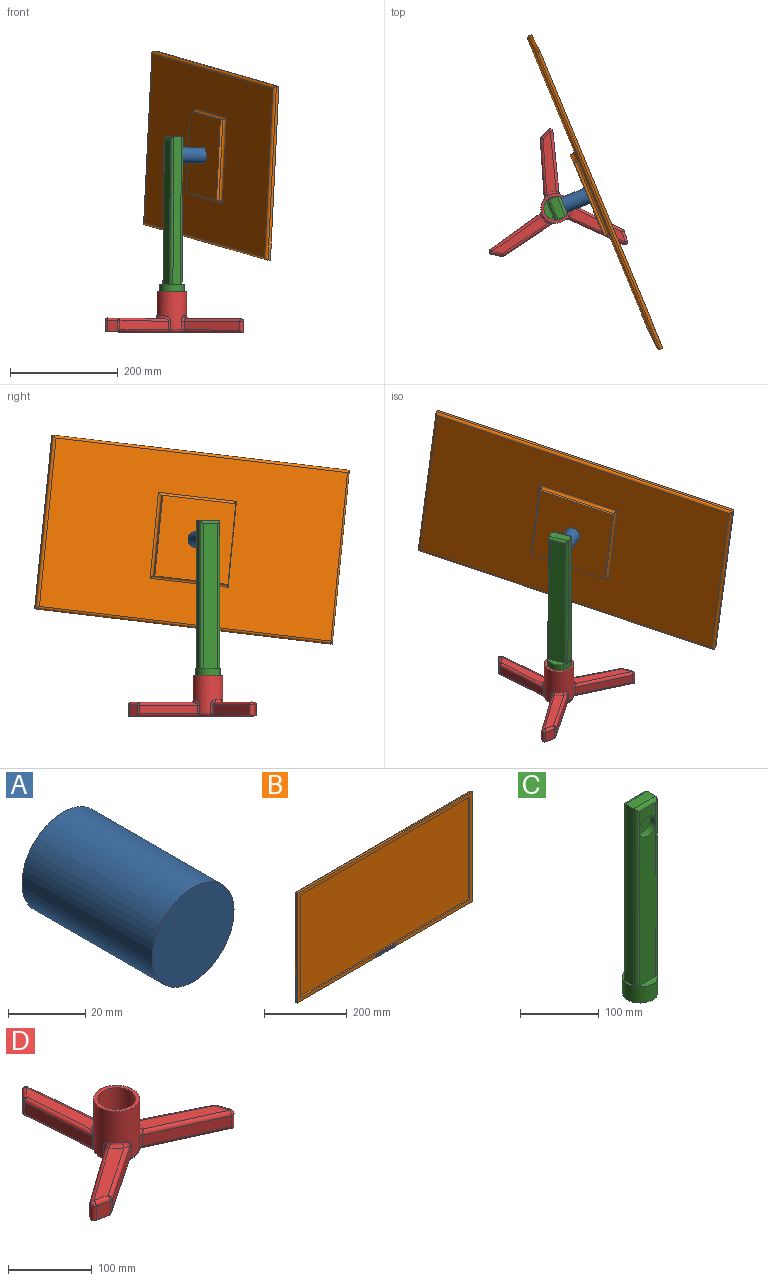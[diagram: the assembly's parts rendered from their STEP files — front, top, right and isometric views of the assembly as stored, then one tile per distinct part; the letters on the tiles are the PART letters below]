
ASSEMBLY  parts=4 mates=3
PART A: 3 faces, bbox 30x47.7x30 mm
  f0: cylinder r=15mm len=47.7mm, axis (0,1,0), area 4495.6mm2, adj f1,f2
  f1: plane 30x30mm, normal (0,-1,0), area 706.9mm2, adj f0
  f2: plane 30x30mm, normal (0,1,0), area 706.9mm2, adj f0
PART B: 199 faces, bbox 600.6x21x326.2 mm
  f0: plane 590.61x316.14mm, normal (0,1,0), area 160454.4mm2, adj f191,f192,f193,f194,f195,f196,f197,f198
  f1: plane 580x5mm, normal (0,0,-1), area 2900mm2, adj f2,f8,f9,f10
  f2: plane 305x5mm, normal (-1,0,0), area 1525mm2, adj f1,f3,f9,f10
  f3: plane 580x5mm, normal (0,0,1), area 2900mm2, adj f2,f8,f9,f10
  f4: plane 325x5mm, normal (1,0,0), area 1625mm2, adj f5,f7,f9,f196
  f5: plane 600x5mm, normal (0,0,1), area 3000mm2, adj f4,f6,f9,f195
  f6: plane 325x5mm, normal (-1,0,0), area 1625mm2, adj f5,f7,f9,f197
  f7: plane 600x5mm, normal (0,0,-1), area 3000mm2, adj f4,f6,f9,f198
  f8: plane 305x5mm, normal (1,0,0), area 1525mm2, adj f1,f3,f9,f10
  f9: plane 600.63x326.16mm, normal (0,-1,0), area 17876.4mm2, adj f1,f2,f3,f4,f5,f6,f7,f8
  f10: plane 580.59x306.12mm, normal (0,-1,0), area 176900mm2, adj f1,f2,f3,f8
  f11: plane 4.15x3.06mm, normal (0.8,0,0.59), area 5.2mm2, adj f9,f12,f22,f23
  f12: plane 3.18x2.95mm, normal (0.73,0,-0.68), area 4.3mm2, adj f9,f11,f13,f23
  f13: plane 1.01x1mm, normal (0,0,1), area 1mm2, adj f9,f12,f14,f23
  f14: plane 3.63x3.32mm, normal (-0.74,0,0.67), area 4.9mm2, adj f9,f13,f15,f23
  f15: plane 3.63x1mm, normal (1,0,0), area 3.6mm2, adj f9,f14,f16,f23
  f16: plane 1x0.85mm, normal (0,0,1), area 0.9mm2, adj f9,f15,f17,f23
  f17: plane 7.33x1mm, normal (-1,0,0), area 7.3mm2, adj f9,f16,f18,f23
  f18: plane 1x0.85mm, normal (0,0,-1), area 0.9mm2, adj f9,f17,f19,f23
  f19: plane 2.87x1mm, normal (1,0,0), area 2.9mm2, adj f9,f18,f20,f23
  f20: plane 1x0.77mm, normal (0.66,0,-0.75), area 1mm2, adj f9,f19,f21,f23
  f21: plane 3.55x2.67mm, normal (-0.8,0,-0.6), area 4.4mm2, adj f9,f20,f22,f23
  f22: plane 1x1mm, normal (0,0,-1), area 1mm2, adj f9,f11,f21,f23
  f23: plane 7.33x5.29mm, normal (0,-1,0), area 14.2mm2, adj f11,f12,f13,f14,f15,f16,f17,f18
  f24: plane 1x0.76mm, normal (-1,0,0), area 0.8mm2, adj f9,f25,f43,f44
  f25: plane 1.64x1mm, normal (0,0,-1), area 1.6mm2, adj f9,f24,f26,f44
  f26: plane 2.26x1mm, normal (-1,0,0), area 2.3mm2, adj f9,f25,f27,f44
  f27: extruded ~1.49x1mm, area 1.5mm2, adj f9,f26,f28,f44
  f28: extruded ~2.13x1mm, area 2.3mm2, adj f9,f27,f29,f44
  f29: extruded ~2.25x1mm, area 2.4mm2, adj f9,f28,f30,f44
  f30: extruded ~2.21x1mm, area 2.4mm2, adj f9,f29,f31,f44
  f31: extruded ~2.09x1mm, area 2.3mm2, adj f9,f30,f32,f44
  f32: extruded ~1.91x1mm, area 2mm2, adj f9,f31,f33,f44
  f33: plane 1x0.75mm, normal (0.92,0,-0.4), area 0.8mm2, adj f9,f32,f34,f44
  f34: extruded ~2.19x1mm, area 2.2mm2, adj f9,f33,f35,f44
  f35: extruded ~2.02x1mm, area 2.1mm2, adj f9,f34,f36,f44
  f36: extruded ~1.32x1.31mm, area 1.9mm2, adj f9,f35,f37,f44
  f37: extruded ~2x1mm, area 2.1mm2, adj f9,f36,f38,f44
  f38: extruded ~2.77x1mm, area 3mm2, adj f9,f37,f39,f44
  f39: extruded ~2.59x1mm, area 2.9mm2, adj f9,f38,f40,f44
  f40: extruded ~1.39x1mm, area 1.4mm2, adj f9,f39,f41,f44
  f41: extruded ~1.18x1mm, area 1.2mm2, adj f9,f40,f42,f44
  f42: plane 3.56x1mm, normal (1,0,0), area 3.6mm2, adj f9,f41,f43,f44
  f43: plane 2.49x1mm, normal (0,0,1), area 2.5mm2, adj f9,f24,f42,f44
  f44: plane 7.53x6.1mm, normal (0,-1,0), area 16.3mm2, adj f24,f25,f26,f27,f28,f29,f30,f31
  f45: plane 7.33x1mm, normal (-1,0,0), area 7.3mm2, adj f9,f46,f69,f70
  f46: plane 2.56x1mm, normal (0,0,-1), area 2.6mm2, adj f9,f45,f47,f70
  f47: extruded ~1.86x1mm, area 2mm2, adj f9,f46,f48,f70
  f48: extruded ~1.53x1mm, area 1.7mm2, adj f9,f47,f49,f70
  f49: extruded ~1.76x1.67mm, area 2.7mm2, adj f9,f48,f50,f70
  f50: plane 1x0.05mm, normal (1,0,0), area 0mm2, adj f9,f49,f51,f70
  f51: extruded ~1.06x1mm, area 1.2mm2, adj f9,f50,f52,f70
  f52: extruded ~1.08x1mm, area 1.2mm2, adj f9,f51,f53,f70
  f53: extruded ~1.38x1mm, area 1.6mm2, adj f9,f52,f54,f70
  f54: extruded ~2.11x1mm, area 2.2mm2, adj f9,f53,f69,f70
  f55: plane 2.4x1mm, normal (1,0,0), area 2.4mm2, adj f56,f67,f70,f72
  f56: plane 1.25x1mm, normal (0,0,-1), area 1.3mm2, adj f55,f57,f70,f72
  f57: extruded ~1.4x1mm, area 1.4mm2, adj f56,f58,f70,f72
  f58: extruded ~1x0.89mm, area 1mm2, adj f57,f59,f70,f72
  f59: extruded ~1x0.95mm, area 1.1mm2, adj f58,f60,f70,f72
  f60: extruded ~1.3x1mm, area 1.3mm2, adj f59,f67,f70,f72
  f61: plane 1.46x1mm, normal (0,0,-1), area 1.5mm2, adj f62,f68,f70,f71
  f62: extruded ~1.4x1mm, area 1.5mm2, adj f61,f63,f70,f71
  f63: extruded ~1x1mm, area 1.1mm2, adj f62,f64,f70,f71
  f64: extruded ~1.08x1mm, area 1.2mm2, adj f63,f65,f70,f71
  f65: extruded ~1.34x1mm, area 1.4mm2, adj f64,f66,f70,f71
  f66: plane 1.53x1mm, normal (0,0,1), area 1.5mm2, adj f65,f68,f70,f71
  f67: plane 1.4x1mm, normal (0,0,1), area 1.4mm2, adj f55,f60,f70,f72
  f68: plane 2.74x1mm, normal (1,0,0), area 2.7mm2, adj f61,f66,f70,f71
  f69: plane 2.07x1mm, normal (0,0,1), area 2.1mm2, adj f9,f45,f54,f70
  f70: plane 7.33x5.08mm, normal (0,-1,0), area 18.3mm2, adj f45,f46,f47,f48,f49,f50,f51,f52
  f71: plane 3.31x2.74mm, normal (0,-1,0), area 8.3mm2, adj f61,f62,f63,f64,f65,f66,f68
  f72: plane 3.1x2.4mm, normal (0,-1,0), area 6.8mm2, adj f55,f56,f57,f58,f59,f60,f67
  f73: extruded ~2.75x2.14mm, area 4mm2, adj f9,f74,f87,f88
  f74: plane 1.9x1mm, normal (0,0,1), area 1.9mm2, adj f9,f73,f75,f88
  f75: plane 7.33x1mm, normal (-1,0,0), area 7.3mm2, adj f9,f74,f76,f88
  f76: plane 1x0.85mm, normal (0,0,-1), area 0.9mm2, adj f9,f75,f77,f88
  f77: plane 2.88x1mm, normal (1,0,0), area 2.9mm2, adj f9,f76,f78,f88
  f78: plane 1x0.86mm, normal (0,0,-1), area 0.9mm2, adj f9,f77,f79,f88
  f79: extruded ~2.17x1mm, area 2.3mm2, adj f9,f78,f87,f88
  f80: plane 2.98x1mm, normal (1,0,0), area 3mm2, adj f81,f86,f88,f89
  f81: plane 1x0.95mm, normal (0,0,-1), area 1mm2, adj f80,f82,f88,f89
  f82: extruded ~1.48x1mm, area 1.6mm2, adj f81,f83,f88,f89
  f83: extruded ~1.08x1mm, area 1.2mm2, adj f82,f84,f88,f89
  f84: extruded ~1.17x1mm, area 1.3mm2, adj f83,f85,f88,f89
  f85: extruded ~1.64x1mm, area 1.7mm2, adj f84,f86,f88,f89
  f86: plane 1x0.77mm, normal (0,0,1), area 0.8mm2, adj f80,f85,f88,f89
  f87: extruded ~1.71x1mm, area 1.9mm2, adj f9,f73,f79,f88
  f88: plane 7.33x4.65mm, normal (0,-1,0), area 13.2mm2, adj f73,f74,f75,f76,f77,f78,f79,f80
  f89: plane 2.98x2.91mm, normal (0,-1,0), area 7.7mm2, adj f80,f81,f82,f83,f84,f85,f86
  f90: plane 1.53x1mm, normal (0,0,-1), area 1.5mm2, adj f9,f91,f107,f108
  f91: plane 3.05x1.77mm, normal (-0.86,0,-0.5), area 3.5mm2, adj f9,f90,f92,f108
  f92: plane 1.01x1mm, normal (0,0,-1), area 1mm2, adj f9,f91,f93,f108
  f93: plane 3.29x1.99mm, normal (0.86,0,0.52), area 3.8mm2, adj f9,f92,f94,f108
  f94: extruded ~1.97x1.47mm, area 2.6mm2, adj f9,f93,f95,f108
  f95: extruded ~1.55x1mm, area 1.7mm2, adj f9,f94,f96,f108
  f96: extruded ~1.99x1mm, area 2.1mm2, adj f9,f95,f97,f108
  f97: plane 2.01x1mm, normal (0,0,1), area 2mm2, adj f9,f96,f98,f108
  f98: plane 7.33x1mm, normal (-1,0,0), area 7.3mm2, adj f9,f97,f99,f108
  f99: plane 1x0.85mm, normal (0,0,-1), area 0.9mm2, adj f9,f98,f107,f108
  f100: plane 2.8x1mm, normal (1,0,0), area 2.8mm2, adj f101,f106,f108,f109
  f101: plane 1.11x1mm, normal (0,0,-1), area 1.1mm2, adj f100,f102,f108,f109
  f102: extruded ~1.38x1mm, area 1.4mm2, adj f101,f103,f108,f109
  f103: extruded ~1.05x1mm, area 1.2mm2, adj f102,f104,f108,f109
  f104: extruded ~1.08x1mm, area 1.2mm2, adj f103,f105,f108,f109
  f105: extruded ~1.32x1mm, area 1.4mm2, adj f104,f106,f108,f109
  f106: plane 1.17x1mm, normal (0,0,1), area 1.2mm2, adj f100,f105,f108,f109
  f107: plane 3.05x1mm, normal (1,0,0), area 3mm2, adj f9,f90,f99,f108
  f108: plane 7.33x5.16mm, normal (0,-1,0), area 16.1mm2, adj f90,f91,f92,f93,f94,f95,f96,f97
  f109: plane 2.91x2.8mm, normal (0,-1,0), area 7.4mm2, adj f100,f101,f102,f103,f104,f105,f106
  f110: extruded ~2.77x1mm, area 3mm2, adj f9,f111,f125,f126
  f111: extruded ~2.47x1mm, area 2.7mm2, adj f9,f110,f112,f126
  f112: extruded ~2.51x1mm, area 2.8mm2, adj f9,f111,f113,f126
  f113: extruded ~2.78x1mm, area 3mm2, adj f9,f112,f114,f126
  f114: extruded ~2.8x1mm, area 3mm2, adj f9,f113,f115,f126
  f115: extruded ~2.5x1mm, area 2.8mm2, adj f9,f114,f116,f126
  f116: extruded ~2.47x1.01mm, area 2.8mm2, adj f9,f115,f125,f126
  f117: extruded ~2.24x1mm, area 2.4mm2, adj f118,f124,f126,f127
  f118: extruded ~1.85x1mm, area 2.1mm2, adj f117,f119,f126,f127
  f119: extruded ~1.83x1mm, area 2.1mm2, adj f118,f120,f126,f127
  f120: extruded ~2.24x1mm, area 2.4mm2, adj f119,f121,f126,f127
  f121: extruded ~2.26x1mm, area 2.4mm2, adj f120,f122,f126,f127
  f122: extruded ~1.84x1mm, area 2.1mm2, adj f121,f123,f126,f127
  f123: extruded ~1.84x1mm, area 2.1mm2, adj f122,f124,f126,f127
  f124: extruded ~2.26x1mm, area 2.4mm2, adj f117,f123,f126,f127
  f125: extruded ~2.77x1mm, area 3mm2, adj f9,f110,f116,f126
  f126: plane 7.55x6.74mm, normal (0,-1,0), area 17mm2, adj f110,f111,f112,f113,f114,f115,f116,f117
  f127: plane 6.04x4.94mm, normal (0,-1,0), area 24.7mm2, adj f117,f118,f119,f120,f121,f122,f123,f124
  f128: extruded ~2.65x1mm, area 2.9mm2, adj f9,f129,f141,f142
  f129: extruded ~2.66x1mm, area 2.9mm2, adj f9,f128,f130,f142
  f130: plane 2.25x1mm, normal (0,0,1), area 2.2mm2, adj f9,f129,f131,f142
  f131: plane 7.33x1mm, normal (-1,0,0), area 7.3mm2, adj f9,f130,f132,f142
  f132: plane 2.03x1mm, normal (0,0,-1), area 2mm2, adj f9,f131,f133,f142
  f133: extruded ~2.83x1mm, area 3.1mm2, adj f9,f132,f141,f142
  f134: extruded ~2.22x1mm, area 2.4mm2, adj f135,f140,f142,f143
  f135: extruded ~2.29x1mm, area 2.5mm2, adj f134,f136,f142,f143
  f136: plane 1.04x1mm, normal (0,0,1), area 1mm2, adj f135,f137,f142,f143
  f137: plane 5.85x1mm, normal (1,0,0), area 5.9mm2, adj f136,f138,f142,f143
  f138: plane 1.24x1mm, normal (0,0,-1), area 1.2mm2, adj f137,f139,f142,f143
  f139: extruded ~2.14x1mm, area 2.3mm2, adj f138,f140,f142,f143
  f140: extruded ~2.16x1mm, area 2.3mm2, adj f134,f139,f142,f143
  f141: extruded ~2.77x1mm, area 3mm2, adj f9,f128,f133,f142
  f142: plane 7.33x5.85mm, normal (0,-1,0), area 17mm2, adj f128,f129,f130,f131,f132,f133,f134,f135
  f143: plane 5.85x4.1mm, normal (0,-1,0), area 21.1mm2, adj f134,f135,f136,f137,f138,f139,f140
  f144: plane 1x0.85mm, normal (0,0,1), area 0.9mm2, adj f9,f145,f157,f158
  f145: plane 4.77x1mm, normal (-1,0,0), area 4.8mm2, adj f9,f144,f146,f158
  f146: extruded ~1.42x1mm, area 1.5mm2, adj f9,f145,f147,f158
  f147: extruded ~1.43x1mm, area 1.6mm2, adj f9,f146,f148,f158
  f148: extruded ~1.47x1mm, area 1.6mm2, adj f9,f147,f149,f158
  f149: extruded ~1.41x1mm, area 1.5mm2, adj f9,f148,f150,f158
  f150: plane 4.78x1mm, normal (1,0,0), area 4.8mm2, adj f9,f149,f151,f158
  f151: plane 1x0.85mm, normal (0,0,1), area 0.9mm2, adj f9,f150,f152,f158
  f152: plane 4.72x1mm, normal (-1,0,0), area 4.7mm2, adj f9,f151,f153,f158
  f153: extruded ~1.99x1mm, area 2.2mm2, adj f9,f152,f154,f158
  f154: extruded ~2.05x1mm, area 2.2mm2, adj f9,f153,f155,f158
  f155: extruded ~2.08x1mm, area 2.3mm2, adj f9,f154,f156,f158
  f156: extruded ~1.97x1mm, area 2.2mm2, adj f9,f155,f157,f158
  f157: plane 4.74x1mm, normal (1,0,0), area 4.7mm2, adj f9,f144,f156,f158
  f158: plane 7.43x5.61mm, normal (0,-1,0), area 14.1mm2, adj f144,f145,f146,f147,f148,f149,f150,f151
  f159: extruded ~1.67x1mm, area 1.7mm2, adj f9,f160,f173,f174
  f160: plane 1x0.73mm, normal (0.9,0,-0.44), area 0.8mm2, adj f9,f159,f161,f174
  f161: extruded ~2.01x1mm, area 2.1mm2, adj f9,f160,f162,f174
  f162: extruded ~1.88x1mm, area 2mm2, adj f9,f161,f163,f174
  f163: extruded ~1.31x1.22mm, area 1.8mm2, adj f9,f162,f164,f174
  f164: extruded ~1.98x1mm, area 2mm2, adj f9,f163,f165,f174
  f165: extruded ~2.79x1mm, area 3mm2, adj f9,f164,f166,f174
  f166: extruded ~2.5x1mm, area 2.8mm2, adj f9,f165,f167,f174
  f167: extruded ~1.88x1mm, area 1.9mm2, adj f9,f166,f168,f174
  f168: plane 1x0.75mm, normal (1,0,0), area 0.7mm2, adj f9,f167,f169,f174
  f169: extruded ~1.75x1mm, area 1.8mm2, adj f9,f168,f170,f174
  f170: extruded ~1.92x1mm, area 2.1mm2, adj f9,f169,f171,f174
  f171: extruded ~2.22x1mm, area 2.4mm2, adj f9,f170,f172,f174
  f172: extruded ~2.2x1mm, area 2.4mm2, adj f9,f171,f173,f174
  f173: extruded ~1.91x1mm, area 2.1mm2, adj f9,f159,f172,f174
  f174: plane 7.53x5.54mm, normal (0,-1,0), area 11.7mm2, adj f159,f160,f161,f162,f163,f164,f165,f166
  f175: plane 6.57x1mm, normal (1,0,0), area 6.6mm2, adj f9,f176,f182,f183
  f176: plane 2.32x1mm, normal (0,0,-1), area 2.3mm2, adj f9,f175,f177,f183
  f177: plane 1x0.76mm, normal (1,0,0), area 0.8mm2, adj f9,f176,f178,f183
  f178: plane 5.49x1mm, normal (0,0,1), area 5.5mm2, adj f9,f177,f179,f183
  f179: plane 1x0.76mm, normal (-1,0,0), area 0.8mm2, adj f9,f178,f180,f183
  f180: plane 2.32x1mm, normal (0,0,-1), area 2.3mm2, adj f9,f179,f181,f183
  f181: plane 6.57x1mm, normal (-1,0,0), area 6.6mm2, adj f9,f180,f182,f183
  f182: plane 1x0.85mm, normal (0,0,-1), area 0.9mm2, adj f9,f175,f181,f183
  f183: plane 7.33x5.49mm, normal (0,-1,0), area 9.8mm2, adj f175,f176,f177,f178,f179,f180,f181,f182
  f184: plane 147.83x5mm, normal (0,0,-1), area 739.1mm2, adj f185,f187,f188,f191
  f185: plane 150.91x5mm, normal (1,0,0), area 754.5mm2, adj f184,f186,f188,f192
  f186: plane 147.83x5mm, normal (0,0,1), area 739.1mm2, adj f185,f187,f188,f194
  f187: plane 150.91x5mm, normal (-1,0,0), area 754.5mm2, adj f184,f186,f188,f193
  f188: plane 150.91x147.83mm, normal (0,1,0), area 21601.4mm2, adj f184,f185,f186,f187,f189
  f189: cylinder r=15mm len=30mm, axis (0,1,0), area 942.5mm2, adj f188,f190
  f190: plane 30x30mm, normal (0,1,0), area 706.9mm2, adj f189
  f191: cylinder r=5mm len=157.83mm, axis (1,0,0), area 1189.6mm2, adj f0,f184,f192,f193
  f192: cylinder r=5mm len=160.91mm, axis (0,0,1), area 1213.8mm2, adj f0,f185,f191,f194
  f193: cylinder r=5mm len=160.91mm, axis (0,0,-1), area 1213.8mm2, adj f0,f187,f191,f194
  f194: cylinder r=5mm len=157.83mm, axis (-1,0,0), area 1189.6mm2, adj f0,f186,f192,f193
  f195: cylinder r=5mm len=600.01mm, axis (-1,0,0), area 4683.8mm2, adj f0,f5,f196,f197
  f196: cylinder r=5mm len=325.01mm, axis (0,0,1), area 2524mm2, adj f0,f4,f195,f198
  f197: cylinder r=5mm len=325.01mm, axis (0,0,-1), area 2524mm2, adj f0,f6,f195,f198
  f198: cylinder r=5mm len=600.01mm, axis (1,0,0), area 4683.8mm2, adj f0,f7,f196,f197
PART C: 17 faces, bbox 45.1x45.1x300 mm
  f0: plane 240.3x30mm, normal (0,-1,0), area 6855.5mm2, adj f6,f7,f10,f15
  f1: plane 275x15mm, normal (-1,0,0), area 4125mm2, adj f5,f7,f8,f15
  f2: plane 275x15mm, normal (1,0,0), area 4125mm2, adj f4,f6,f8,f15
  f3: plane 270x30mm, normal (0,1,0), area 8100mm2, adj f4,f5,f12,f15
  f4: cylinder r=5mm len=275mm, axis (0,0,-1), area 2145.6mm2, adj f2,f3,f12,f15
  f5: cylinder r=5mm len=275mm, axis (0,0,1), area 2145.6mm2, adj f1,f3,f12,f15
  f6: cylinder r=5mm len=275mm, axis (0,0,1), area 2145.6mm2, adj f0,f2,f9,f13,f15
  f7: cylinder r=5mm len=275mm, axis (0,0,-1), area 2145.6mm2, adj f0,f1,f9,f13,f15
  f8: plane 40x15mm, normal (0,0,1), area 600mm2, adj f1,f2,f12,f13
  f9: plane 30x29.7mm, normal (0,-1,0), area 537.7mm2, adj f6,f7,f10,f13
  f10: cylinder r=15mm len=30mm, axis (0,-1,0), area 942.5mm2, adj f0,f9,f11
  f11: plane 30x30mm, normal (0,-1,0), area 706.9mm2, adj f10
  f12: cylinder r=5mm len=40mm, axis (1,0,0), area 285.6mm2, adj f3,f4,f5,f8
  f13: cylinder r=5mm len=40mm, axis (-1,0,0), area 285.6mm2, adj f6,f7,f8,f9
  f14: cylinder r=22.55mm len=45.1mm, axis (0,0,-1), area 3541.9mm2, adj f15,f16
  f15: plane 45.1x45.1mm, normal (0,0,1), area 618.8mm2, adj f0,f1,f2,f3,f4,f5,f6,f7
  f16: plane 45.1x45.1mm, normal (0,0,-1), area 1597.3mm2, adj f14
PART D: 69 faces, bbox 259.7x241x76.3 mm
  f0: plane 120.41x84.17mm, normal (0,0,-1), area 1994.7mm2, adj f14,f15,f44,f49,f66,f67,f68
  f1: plane 119.23x73.88mm, normal (0,0,-1), area 1994.7mm2, adj f8,f15,f23,f28,f30,f34,f37
  f2: plane 134.67x31.56mm, normal (0,0,-1), area 1994.7mm2, adj f11,f15,f31,f35,f36,f55,f59
  f3: plane 103.05x68.66mm, normal (0,0,1), area 1697.8mm2, adj f53,f57,f61,f62
  f4: plane 115.12x24.21mm, normal (0,0,1), area 1697.8mm2, adj f39,f42,f46,f47
  f5: plane 90.07x60.33mm, normal (0.56,-0.83,0), area 1723.7mm2, adj f48,f49,f53,f54
  f6: cylinder r=27.5mm len=71mm, axis (0,0,-1), area 9656.1mm2, adj f17,f21,f24,f25,f29,f32,f33,f40
  f7: plane 103.62x47mm, normal (-0.41,-0.91,0), area 1809mm2, adj f26,f30,f33,f34
  f8: plane 21.18x19.37mm, normal (0.95,0.31,0), area 418mm2, adj f1,f20,f22,f23,f30
  f9: plane 97.28x47.84mm, normal (0.44,0.9,0), area 1723.7mm2, adj f18,f20,f23,f24
  f10: plane 113.23x15.9mm, normal (1,0.1,0), area 1809mm2, adj f31,f35,f39,f40
  f11: plane 21.18x15.29mm, normal (-0.75,0.67,0), area 418mm2, adj f2,f35,f42,f50,f55
  f12: plane 108.17x15.9mm, normal (-1,-0.07,0), area 1723.7mm2, adj f46,f50,f55,f56
  f13: plane 92.51x66.24mm, normal (-0.58,0.81,0), area 1809mm2, adj f61,f64,f67,f68
  f14: plane 21.18x19.97mm, normal (-0.2,-0.98,0), area 418mm2, adj f0,f49,f54,f62,f67
  f15: cylinder r=22.5mm len=76mm, axis (0,0,-1), area 10744.2mm2, adj f0,f1,f2,f17,f32,f41,f63
  f16: plane 101.01x63.37mm, normal (0,0,1), area 1697.8mm2, adj f18,f22,f25,f26
  f17: plane 55x55mm, normal (0,0,1), area 785.4mm2, adj f6,f15
  f18: cylinder r=5mm len=99.49mm, axis (0.9,-0.44,0), area 824.8mm2, adj f9,f16,f19,f21
  f19: sphere r=5mm, area 19.9mm2, adj f18,f20,f22
  f20: cylinder r=5mm len=19.47mm, axis (0,0,-1), area 70.3mm2, adj f8,f9,f19,f23
  f21: bspline ~12.65x10.62mm, area 70.9mm2, adj f6,f18,f24,f25
  f22: cylinder r=5mm len=20.66mm, axis (0.31,-0.95,0), area 157.9mm2, adj f8,f16,f19,f27
  f23: cylinder r=5mm len=105.77mm, axis (-0.9,0.44,0), area 879mm2, adj f1,f8,f9,f20,f28
  f24: cylinder r=5mm len=15.9mm, axis (0,0,-1), area 55.1mm2, adj f6,f9,f21,f28
  f25: torus R=32.5mm, axis (0,0,1), area 130.4mm2, adj f6,f16,f21,f29
  f26: cylinder r=5mm len=105.68mm, axis (-0.91,0.41,0), area 883.6mm2, adj f7,f16,f27,f29
  f27: sphere r=5mm, area 57.9mm2, adj f22,f26,f30
  f28: torus R=10mm, axis (0,0,1), area 37.1mm2, adj f1,f23,f24,f32
  f29: bspline ~12.06x10.38mm, area 70.7mm2, adj f6,f25,f26,f33
  f30: cylinder r=5mm len=20.9mm, axis (0,0,-1), area 227.7mm2, adj f1,f7,f8,f27,f34
  f31: cylinder r=5mm len=118.7mm, axis (-0.1,1,0), area 918.6mm2, adj f2,f10,f35,f36
  f32: torus R=22.5mm, axis (0,0,1), area 163.1mm2, adj f6,f15,f28,f36
  f33: cylinder r=5mm len=15.9mm, axis (0,0,-1), area 90mm2, adj f6,f7,f29,f37
  f34: cylinder r=5mm len=110.23mm, axis (0.91,-0.41,0), area 918.6mm2, adj f1,f7,f30,f37
  f35: cylinder r=5mm len=20.9mm, axis (0,0,-1), area 227.7mm2, adj f2,f10,f11,f31,f38
  f36: torus R=10mm, axis (0,0,1), area 60.6mm2, adj f2,f31,f32,f40
  f37: torus R=10mm, axis (0,0,1), area 60.6mm2, adj f1,f33,f34,f41
  f38: sphere r=5mm, area 58.8mm2, adj f35,f39,f42
  f39: cylinder r=5mm len=113.72mm, axis (0.1,-1,0), area 883.6mm2, adj f4,f10,f38,f43
  f40: cylinder r=5mm len=15.9mm, axis (0,0,-1), area 90mm2, adj f6,f10,f36,f43
  f41: torus R=22.5mm, axis (0,0,1), area 163.1mm2, adj f6,f15,f37,f44
  f42: cylinder r=5mm len=18.33mm, axis (0.67,0.75,0), area 157.9mm2, adj f4,f11,f38,f45
  f43: bspline ~12.06x9.8mm, area 70.7mm2, adj f6,f39,f40,f47
  f44: torus R=10mm, axis (0,0,1), area 37.1mm2, adj f0,f41,f48,f49
  f45: sphere r=5mm, area 19.9mm2, adj f42,f46,f50
  f46: cylinder r=5mm len=108.5mm, axis (-0.07,1,0), area 824.8mm2, adj f4,f12,f45,f51
  f47: torus R=32.5mm, axis (0,0,1), area 130.4mm2, adj f4,f6,f43,f51
  f48: cylinder r=5mm len=15.9mm, axis (0,0,-1), area 55.1mm2, adj f5,f6,f44,f52
  f49: cylinder r=5mm len=98.67mm, axis (0.83,0.56,0), area 879mm2, adj f0,f5,f14,f44,f54
  f50: cylinder r=5mm len=19.47mm, axis (0,0,-1), area 70.3mm2, adj f11,f12,f45,f55
  f51: bspline ~12.76x10.62mm, area 70.9mm2, adj f6,f46,f47,f56
  f52: bspline ~13.18x10.62mm, area 70.9mm2, adj f6,f48,f53,f57
  f53: cylinder r=5mm len=92.85mm, axis (-0.83,-0.56,0), area 824.8mm2, adj f3,f5,f52,f58
  f54: cylinder r=5mm len=19.47mm, axis (0,0,-1), area 70.3mm2, adj f5,f14,f49,f58
  f55: cylinder r=5mm len=115.49mm, axis (0.07,-1,0), area 879mm2, adj f2,f11,f12,f50,f59
  f56: cylinder r=5mm len=15.9mm, axis (0,0,-1), area 55.1mm2, adj f6,f12,f51,f59
  f57: torus R=32.5mm, axis (0,0,1), area 130.4mm2, adj f3,f6,f52,f60
  f58: sphere r=5mm, area 19.9mm2, adj f53,f54,f62
  f59: torus R=10mm, axis (0,0,1), area 37.1mm2, adj f2,f55,f56,f63
  f60: bspline ~12.06x11.33mm, area 70.7mm2, adj f6,f57,f61,f64
  f61: cylinder r=5mm len=95.42mm, axis (0.81,0.58,0), area 883.6mm2, adj f3,f13,f60,f65
  f62: cylinder r=5mm len=20.7mm, axis (-0.98,0.2,0), area 157.9mm2, adj f3,f14,f58,f65
  f63: torus R=22.5mm, axis (0,0,1), area 163.1mm2, adj f6,f15,f59,f66
  f64: cylinder r=5mm len=15.9mm, axis (0,0,-1), area 90mm2, adj f6,f13,f60,f66
  f65: sphere r=5mm, area 57.9mm2, adj f61,f62,f67
  f66: torus R=10mm, axis (0,0,1), area 60.6mm2, adj f0,f63,f64,f68
  f67: cylinder r=5mm len=20.9mm, axis (0,0,-1), area 227.7mm2, adj f0,f13,f14,f65,f68
  f68: cylinder r=5mm len=99.48mm, axis (-0.81,-0.58,0), area 918.6mm2, adj f0,f13,f66,f67
PLACE A rot(axis=(0.64,-0.43,0.64),133.6deg) t=(12.62,48.61,25.91)mm
PLACE B rot(axis=(0.06,-0.03,1),112.6deg) t=(65.91,70.73,25.51)mm
PLACE C rot(axis=(0,0,1),112.5deg) t=(11.52,48.61,-121.89)mm
PLACE D rot(axis=(0,1,0),0.4deg) t=(-2.25,43.46,-303.29)mm fixed
MATE revolute B.f189 <-> A.f0  axis (-0.92,-0.38,0.01) through (56.68,66.9,25.58)mm
MATE slider A.f0 <-> C.f10  axis (-0.92,-0.38,0.01) through (12.62,48.61,25.91)mm
MATE cylindrical C.f14 <-> D.f6  axis (-0.01,0,-1) through (-1.78,43.46,-239.29)mm
